# Revit family: Window-Casement-Fleetwood-2000-C
name_source: partatom
category: Windows
revit_build: Autodesk Revit Architecture 2013 (Build: 20120221_2030(x64)
units: mm (PartAtom-declared; Revit-internal decimal feet)

## types (4) — shared parameters
2nd_Cam_Handle = No
Cam_Height = 18 "
Configuration = C
Default Sill Height = 36 "
Exterior_Wrap = 0.5 "
Frame_Finish = Aluminum, Anodized Clear
Frame_Thickness = 1.75 "
Glazing_Location = 0.4922 "
Glazing_Material = Glass
Glazing_Thickness = 1 "
Hardware_Finish = Stainless Steel, Brushed
Height = 36 "
Hinged_Screen_Height = 34.716 "
Hinged_Screen_Width = 22.56 "
Interior_Wrap = 0.5 "
Manufacturer = Fleetwood Windows and Doors
Model = 2000
Roto_Knob = No
Rough Height = 36.5 "
Rough Width = 24.5 "
Screen_Height = 33.1256 "
Screen_Material = ULTRA_VUE
Screen_Width = 21.1256 "
Shim_Space = 0.25 "
URL = http://www.fleetwoodusa.com
Wall Closure = By host
Width = 24 "

## per-type parameters (varying)
| type | Butt_Hinge | Cam_Handle | FLat_Screen | Folding_Roto | Hinged_Screen | Multi_Point_Lock |
| Cam Handle | No | Yes | No | No | No | No |
| Cam Handle W/ Hinged Screen | No | Yes | No | No | Yes | No |
| Folding Roto | Yes | No | No | Yes | No | Yes |
| Folding Roto W/ Flat screen | Yes | No | Yes | Yes | No | Yes |

## geometry (parser evidence)
native form markers: Blend x10, Sweep x39
no freeform markers — native parametric forms only
